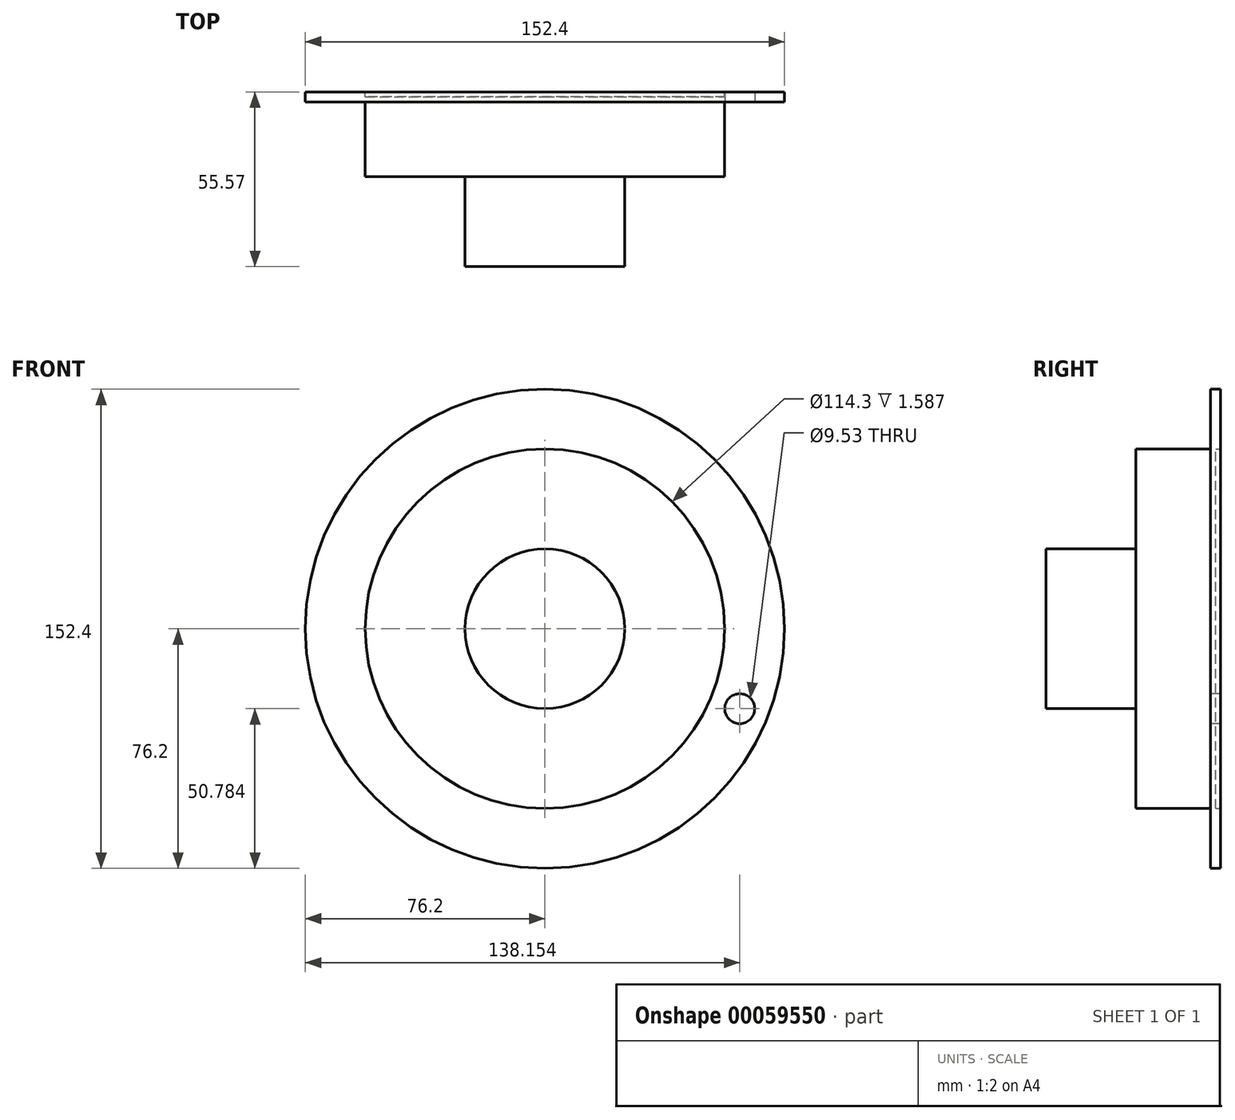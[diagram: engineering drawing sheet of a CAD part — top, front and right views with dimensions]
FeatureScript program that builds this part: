
annotation { "Feature Type Name" : "Feature", "Feature Type Description" : "" }
export const myFeature = defineFeature(function(context is Context, id is Id, definition is map)
    precondition{}
    {
        {
            var Q0;
            Q0=qCreatedBy(makeId("Front.planeOp"),FACE);
            var sketch = newSketch(context, id + "F0", { "sketchPlane" : qUnion([Q0])});
            skCircle(sketch, "E0", {"center": v(0, 0) * mm, "radius": 25.4 * mm});
            skCircle(sketch, "E1", {"center": v(0, 0) * mm, "radius": 57.15 * mm});
            skCircle(sketch, "E2", {"center": v(0, 0) * mm, "radius": 76.2 * mm});
            skSolve(sketch);
        }
        {
            var Q0;
            Q0=makeQuery(id+"F0.imprint","IMPRINT",FACE,{"disambiguationData":[TD([[makeQuery(id+"F0.imprint","IMPRINT",EDGE,{"derivedFrom":sQuery(id+"F0.wireOp",EDGE,"E0")}),-1.0]])]});
            extrude(context, id + "F1", {"entities" : qUnion([Q0]), "depth" : 25.4 * mm});
        }
        {
            var Q0;
            Q0=makeQuery(id+"F0.imprint","IMPRINT",FACE,{"disambiguationData":[TD([[makeQuery(id+"F0.imprint","IMPRINT",EDGE,{"derivedFrom":sQuery(id+"F0.wireOp",EDGE,"E1")}),-1.0]])]});
            extrude(context, id + "F2", {"entities" : qUnion([Q0]), "operationType" : NewBodyOperationType.ADD, "endBound" : BoundingType.SYMMETRIC, "depth" : 3.17 * mm});
        }
        {
            var Q0;
            Q0=makeQuery(id+"F0.imprint","IMPRINT",FACE,{"disambiguationData":[TD([[makeQuery(id+"F0.imprint","IMPRINT",EDGE,{"derivedFrom":sQuery(id+"F0.wireOp",EDGE,"E0")}),1.0]])]});
            extrude(context, id + "F3", {"entities" : qUnion([Q0]), "operationType" : NewBodyOperationType.ADD, "depth" : 53.97 * mm});
        }
        {
            var Q0;
            Q0=makeQuery(id+"F2.opExtrude","CAP_FACE",FACE,{"disambiguationData":[OSD([sQuery(id+"F0.wireOp",EDGE,"E1"),sQuery(id+"F0.wireOp",EDGE,"E2")])],"isStart":false});
            var sketch = newSketch(context, id + "F4", { "sketchPlane" : qUnion([Q0])});
            skCircle(sketch, "E3", {"center": v(61.95, -25.42) * mm, "radius": 4.76 * mm});
            skSolve(sketch);
        }
        {
            var Q0;
            Q0=makeQuery(id+"F4.imprint","IMPRINT",FACE,{"disambiguationData":[TD([[makeQuery(id+"F4.imprint","IMPRINT",EDGE,{"derivedFrom":sQuery(id+"F4.wireOp",EDGE,"E3")}),1.0]])]});
            extrude(context, id + "F5", {"entities" : qUnion([Q0]), "operationType" : NewBodyOperationType.REMOVE, "endBound" : BoundingType.THROUGH_ALL, "oppositeDirection" : true, "depth" : 25.4 * mm});
        }
    });
